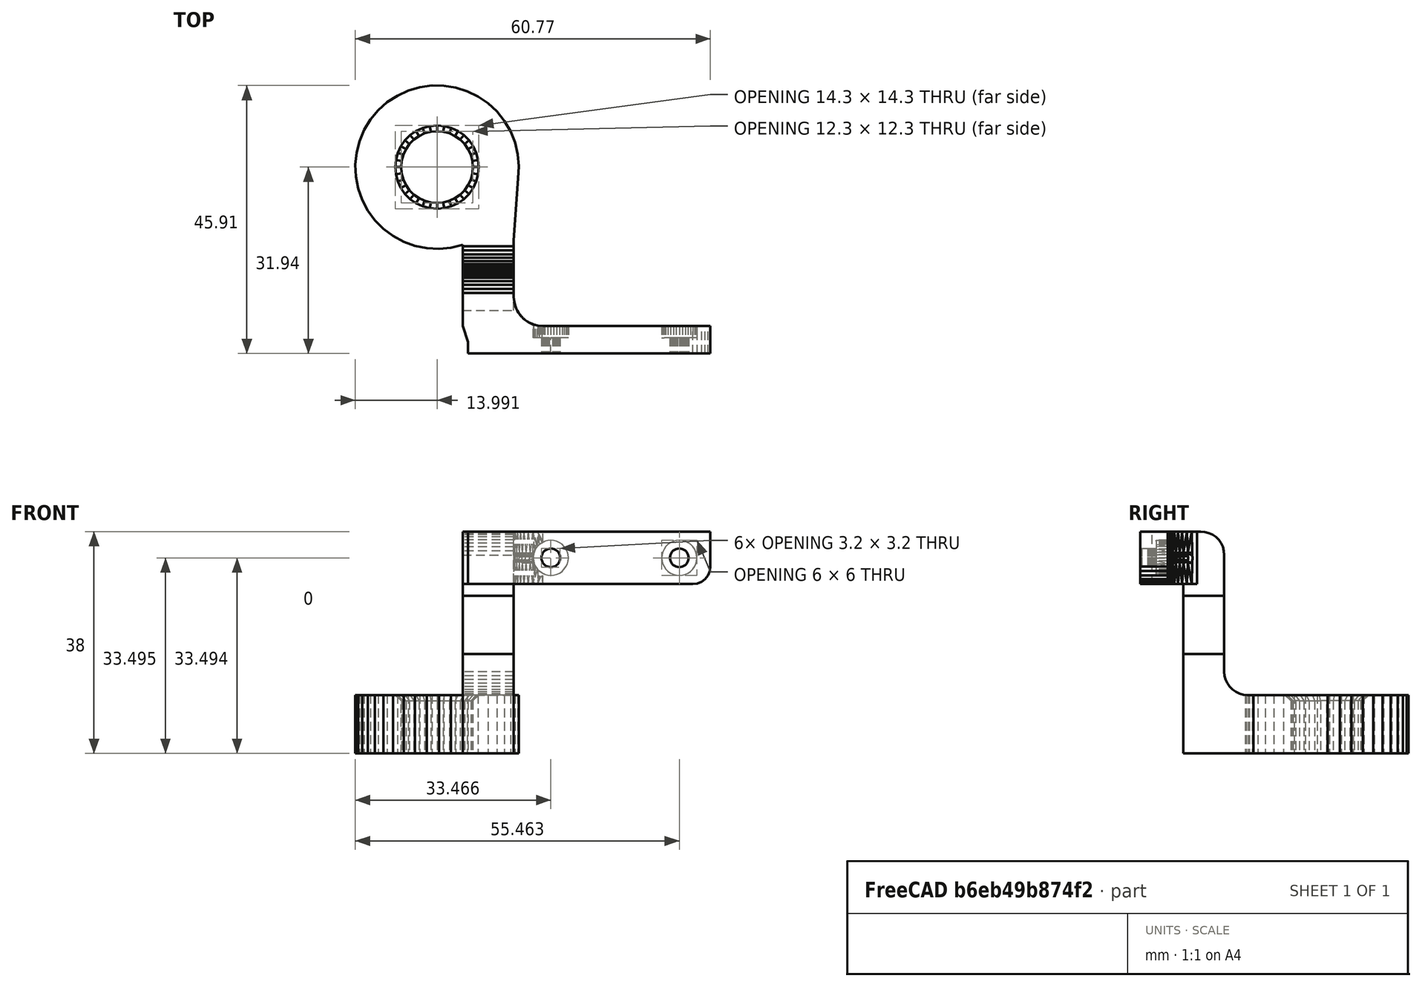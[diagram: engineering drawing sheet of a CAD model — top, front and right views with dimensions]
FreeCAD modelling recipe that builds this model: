
FCSTD DOCUMENT  (FreeCAD 0.15R4671 (Git))
Label: max_support_inductif_capacitif_12mm
License: All rights reserved
LicenseURL: http://en.wikipedia.org/wiki/All_rights_reserved
objects: Part::Feature×10, Part::Box×2, Part::MultiCommon×2, Part::Extrusion×2, Mesh::Feature×1, Part::MultiFuse×1
note: 17 computed .brp shape members not serialized (recipe doc carries the construction recipe); baked Part::Feature solids carry a one-line shape summary decoded from their .brp

FEATURE [Mesh::Feature] support_inductif_capacitif_12mm
FEATURE [Part::Feature] support_inductif_capacitif_12mm001
  shape: bbox 60.77 x 45.91 x 28 mm, 1350 faces, 0 solids (baked)
FEATURE [Part::Feature] support_inductif_capacitif_12mm001001  label="support_inductif_capacitif_12mm002"
  shape: bbox 60.77 x 45.91 x 28 mm, 589 faces, 0 solids (baked)
FEATURE [Part::Feature] support_inductif_capacitif_12mm001001_solid  label="support_inductif_capacitif_12mm002 (Solid)"
  shape: bbox 60.77 x 45.91 x 28 mm, 589 faces (baked)
FEATURE [Part::Box] Box  label="Cube"
  Height = 18
  Length = 70
  Placement = pos=(-1,-1,-1) rot=(0,0,1;0rad)
  Width = 70
FEATURE [Part::MultiCommon] Common  label="bottom"
  Shapes = -> [support_inductif_capacitif_12mm001001_solid,Box]
FEATURE [Part::Feature] support_inductif_capacitif_12mm001001_solid001  label="support_inductif_capacitif_12mm002 (Solid)001"
  shape: bbox 60.77 x 45.91 x 28 mm, 589 faces (baked)
FEATURE [Part::Box] Box001  label="Cube001"
  Height = 18
  Length = 70
  Placement = pos=(-1,-1,17) rot=(0,0,1;0rad)
  Width = 70
FEATURE [Part::MultiCommon] Common001  label="top"
  Placement = pos=(0,0,10) rot=(0,0,1;0rad)
  Shapes = -> [support_inductif_capacitif_12mm001001_solid001,Box001]
FEATURE [Part::Feature] Common_solid  label="bottom (Solid)"
  shape: bbox 27.99 x 38.53 x 17 mm, 159 faces (baked)
FEATURE [Part::Feature] Common001_solid  label="top (Solid)"
  shape: bbox 42.39 x 14.37 x 11 mm, 436 faces (baked)
FEATURE [Part::Feature] Common_solid001  label="bottom (Solid)001"
  shape: bbox 27.99 x 38.53 x 17 mm, 159 faces (baked)
FEATURE [Part::Feature] Common001_solid001  label="top (Solid)001"
  shape: bbox 42.39 x 14.37 x 11 mm, 436 faces (baked)
FEATURE [Part::Feature] Face
  shape: bbox 8.749 x 7 x 2e-07 mm, 1 faces, 0 solids (baked)
FEATURE [Part::Extrusion] Extrude
  Base = -> Face
  Dir = (0,0,10)
  Solid = false
FEATURE [Part::Extrusion] Extrude001
  Base = -> Face
  Dir = (0,0,10)
  Solid = false
FEATURE [Part::MultiFuse] Fusion
  Shapes = -> [Extrude,Common001_solid,Common_solid001]
FEATURE [Part::Feature] Fusion001
  shape: bbox 60.77 x 45.91 x 38 mm, 589 faces (baked)
